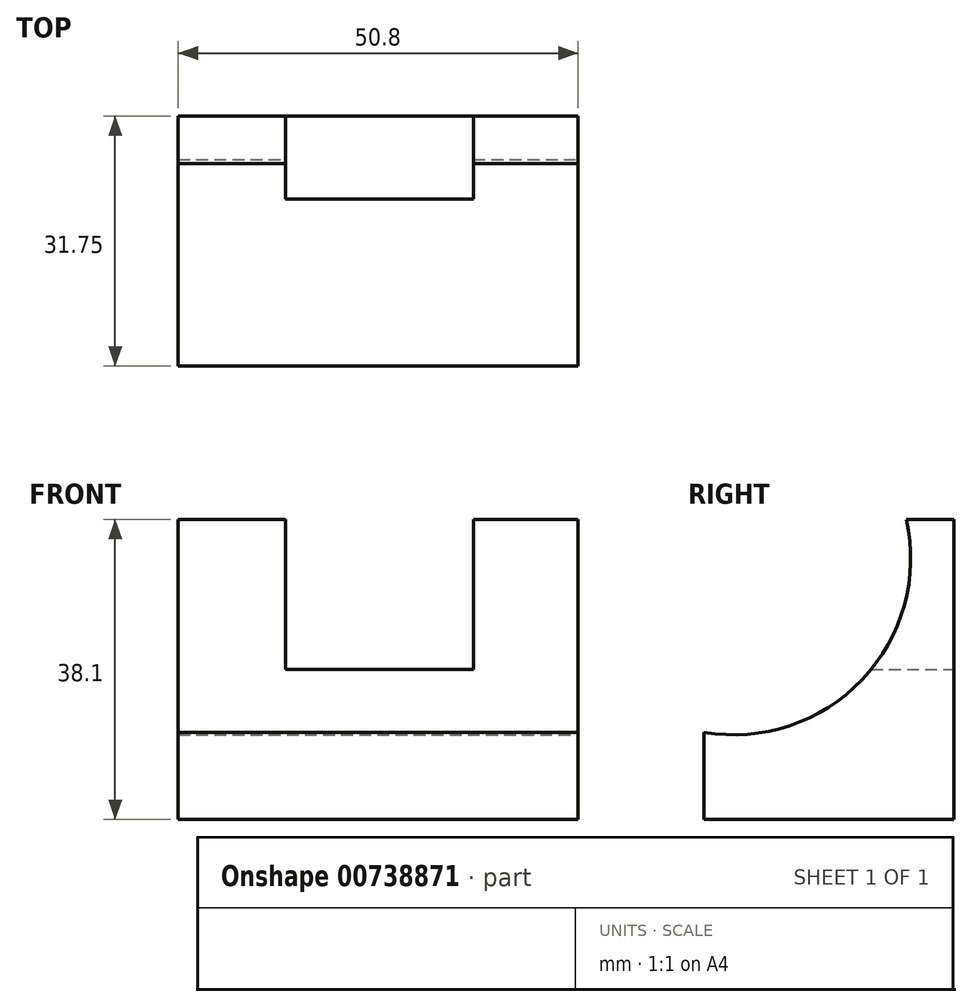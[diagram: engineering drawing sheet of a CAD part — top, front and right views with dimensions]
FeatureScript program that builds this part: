
annotation { "Feature Type Name" : "Feature", "Feature Type Description" : "" }
export const myFeature = defineFeature(function(context is Context, id is Id, definition is map)
    precondition{}
    {
        {
            var Q0;
            Q0=qCreatedBy(makeId("Front.planeOp"),FACE);
            var sketch = newSketch(context, id + "F0", { "sketchPlane" : qUnion([Q0])});
            skLineSegment(sketch, "E0.bottom", {"start": v(-31.45, -5.03) * mm, "end": v(19.35, -5.03) * mm});
            skLineSegment(sketch, "E0.top", {"start": v(-31.45, 33.07) * mm, "end": v(19.35, 33.07) * mm});
            skLineSegment(sketch, "E0.left", {"start": v(-31.45, -5.03) * mm, "end": v(-31.45, 33.07) * mm});
            skLineSegment(sketch, "E0.right", {"start": v(19.35, -5.03) * mm, "end": v(19.35, 33.07) * mm});
            skSolve(sketch);
        }
        {
            var Q0;
            Q0=makeQuery(id+"F0.imprint","IMPRINT",FACE,{"disambiguationData":[TD([[makeQuery(id+"F0.imprint","IMPRINT",EDGE,{"derivedFrom":sQuery(id+"F0.wireOp",EDGE,"E0.bottom")}),1.0]])]});
            extrude(context, id + "F1", {"entities" : qUnion([Q0]), "depth" : 31.75 * mm, "offsetDistance" : 25.4 * mm});
        }
        {
            var Q0;
            Q0=makeQuery(id+"F1.opExtrude","SWEPT_FACE",FACE,{"disambiguationData":[OSD([sQuery(id+"F0.wireOp",EDGE,"E0.right")])]});
            var sketch = newSketch(context, id + "F2", { "sketchPlane" : qUnion([Q0])});
            skArc(sketch, "E1", {"start": v(-31.75, 6.05) * mm, "mid": v(-11.7, 12.7) * mm, "end": v(-6.05, 33.07) * mm});
            skSolve(sketch);
        }
        {
            var Q0;
            {var subQ0=sQuery(id+"F2.wireOp",EDGE,"E1");Q0=makeQuery(id+"F2.imprint","IMPRINT",FACE,{"disambiguationData":[TD([[makeQuery(id+"F2.imprint","IMPRINT",EDGE,{"derivedFrom":subQ0}),1.0]])]});}
            extrude(context, id + "F3", {"entities" : qUnion([Q0]), "operationType" : NewBodyOperationType.REMOVE, "oppositeDirection" : true, "depth" : 50.8 * mm, "offsetDistance" : 25.4 * mm});
        }
        {
            var Q0;
            Q0=makeQuery(id+"F1.opExtrude","SWEPT_FACE",FACE,{"disambiguationData":[OSD([sQuery(id+"F0.wireOp",EDGE,"E0.top")])]});
            var sketch = newSketch(context, id + "F4", { "sketchPlane" : qUnion([Q0])});
            skLineSegment(sketch, "E2.bottom", {"start": v(-12.87, -6.05) * mm, "end": v(6.05, -6.05) * mm});
            skLineSegment(sketch, "E2.top", {"start": v(-12.87, 0) * mm, "end": v(6.05, 0) * mm});
            skLineSegment(sketch, "E2.left", {"start": v(-12.87, -6.05) * mm, "end": v(-12.87, 0) * mm});
            skLineSegment(sketch, "E2.right", {"start": v(6.05, -6.05) * mm, "end": v(6.05, 0) * mm});
            skLineSegment(sketch, "E3.bottom", {"start": v(-12.87, -6.05) * mm, "end": v(-17.83, -6.05) * mm});
            skLineSegment(sketch, "E3.top", {"start": v(-12.87, 0) * mm, "end": v(-17.83, 0) * mm});
            skLineSegment(sketch, "E3.right", {"start": v(-17.83, -6.05) * mm, "end": v(-17.83, 0) * mm});
            skSolve(sketch);
        }
        {
            var Q0;
            Q0=makeQuery(id+"F4.imprint","IMPRINT",FACE,{"disambiguationData":[TD([[makeQuery(id+"F4.imprint","IMPRINT",EDGE,{"derivedFrom":sQuery(id+"F4.wireOp",EDGE,"E2.bottom")}),1.0]])]});
            var Q1;
            Q1=makeQuery(id+"F4.imprint","IMPRINT",FACE,{"disambiguationData":[TD([[makeQuery(id+"F4.imprint","IMPRINT",EDGE,{"derivedFrom":sQuery(id+"F4.wireOp",EDGE,"E3.bottom")}),1.0]])]});
            extrude(context, id + "F5", {"entities" : qUnion([Q0, Q1]), "operationType" : NewBodyOperationType.REMOVE, "oppositeDirection" : true, "depth" : 19.05 * mm, "offsetDistance" : 25.4 * mm});
        }
        {
            var Q0;
            Q0=makeQuery(id+"F5.boolean.opBoolean","COPY",FACE,{"derivedFrom":makeQuery(id+"F5.opExtrude","SWEPT_FACE",FACE,{"disambiguationData":[OSD([sQuery(id+"F4.wireOp",EDGE,"E2.bottom"),sQuery(id+"F4.wireOp",EDGE,"E3.bottom")])]})});
            extrude(context, id + "F6", {"entities" : qUnion([Q0]), "operationType" : NewBodyOperationType.REMOVE, "oppositeDirection" : true, "depth" : 25.4 * mm, "offsetDistance" : 25.4 * mm});
        }
    });
